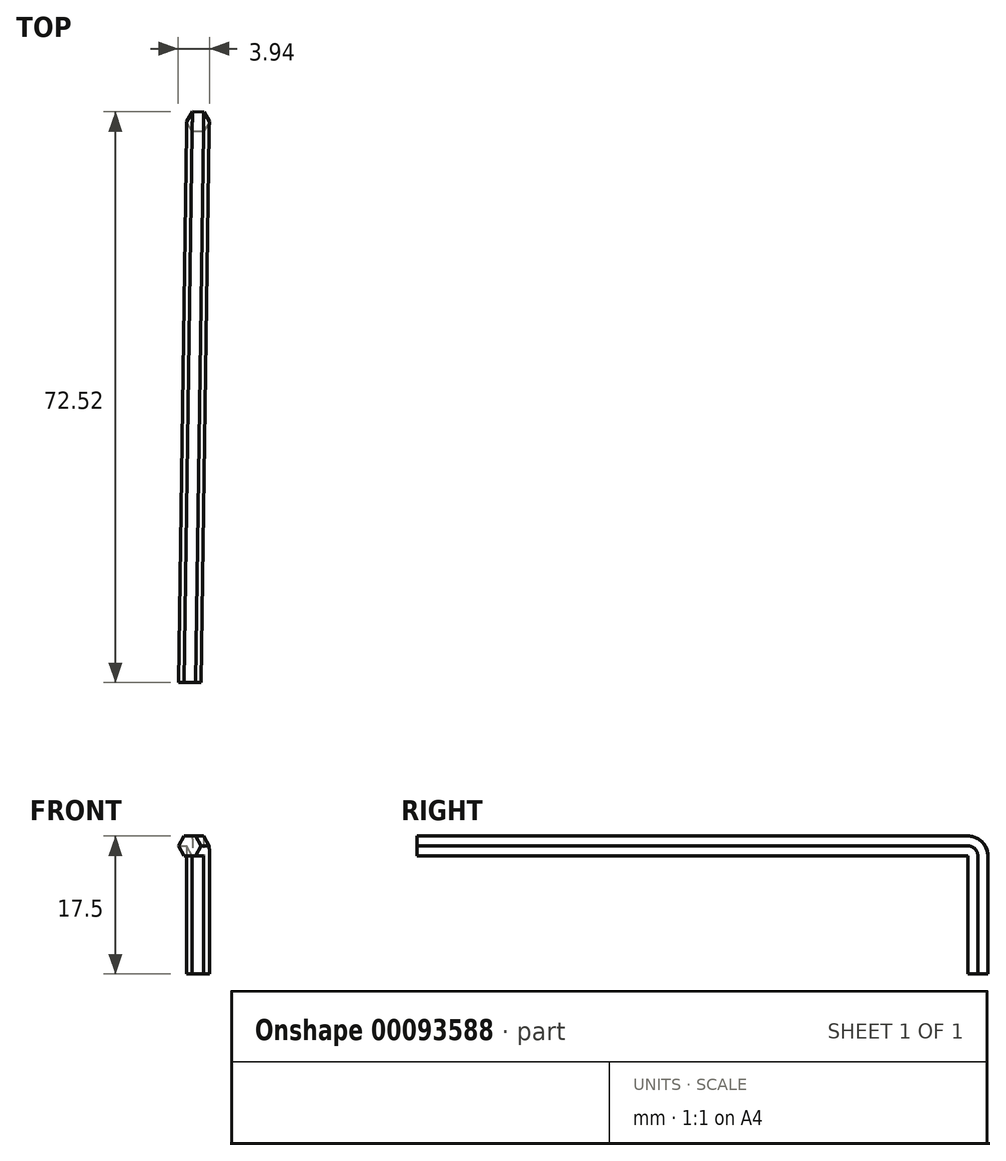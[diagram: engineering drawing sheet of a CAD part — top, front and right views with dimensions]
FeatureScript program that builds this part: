
annotation { "Feature Type Name" : "Feature", "Feature Type Description" : "" }
export const myFeature = defineFeature(function(context is Context, id is Id, definition is map)
    precondition{}
    {
        {
            var Q0;
            Q0=qCreatedBy(makeId("Top.planeOp"),FACE);
            var sketch = newSketch(context, id + "F0", { "sketchPlane" : qUnion([Q0])});
            skCircle(sketch, "E0.cCircle", {"center": v(0, 0) * mm, "radius": 1.25 * mm, "construction": true});
            skLineSegment(sketch, "E0.0", {"start": v(1.44, -0.02) * mm, "end": v(0.7, -1.26) * mm});
            skLineSegment(sketch, "E0.1", {"start": v(0.7, -1.26) * mm, "end": v(-0.74, -1.24) * mm});
            skLineSegment(sketch, "E0.2", {"start": v(-0.74, -1.24) * mm, "end": v(-1.44, 0.02) * mm});
            skLineSegment(sketch, "E0.3", {"start": v(-1.44, 0.02) * mm, "end": v(-0.7, 1.26) * mm});
            skLineSegment(sketch, "E0.4", {"start": v(-0.7, 1.26) * mm, "end": v(0.74, 1.24) * mm});
            skLineSegment(sketch, "E0.5", {"start": v(0.74, 1.24) * mm, "end": v(1.44, -0.02) * mm});
            skPoint(sketch, "E0.0.midPoint", {"position": v(1.07, -0.64) * mm});
            skSolve(sketch);
        }
        {
            var Q0;
            Q0=makeQuery(id+"F0.imprint","IMPRINT",FACE,{"disambiguationData":[TD([[makeQuery(id+"F0.imprint","IMPRINT",EDGE,{"derivedFrom":sQuery(id+"F0.wireOp",EDGE,"E0.0")}),-1.0]])]});
            extrude(context, id + "F1", {"entities" : qUnion([Q0]), "depth" : 15 * mm});
        }
        {
            var Q0;
            Q0=makeQuery(id+"F1.opExtrude","CAP_FACE",FACE,{"disambiguationData":[OSD([sQuery(id+"F0.wireOp",EDGE,"E0.0"),sQuery(id+"F0.wireOp",EDGE,"E0.1"),sQuery(id+"F0.wireOp",EDGE,"E0.2"),sQuery(id+"F0.wireOp",EDGE,"E0.3"),sQuery(id+"F0.wireOp",EDGE,"E0.4"),sQuery(id+"F0.wireOp",EDGE,"E0.5")])],"isStart":false});
            var sketch = newSketch(context, id + "F2", { "sketchPlane" : qUnion([Q0])});
            skSolve(sketch);
        }
        {
            var Q0;
            Q0=makeQuery(id+"F2.imprint","IMPRINT",FACE,{"disambiguationData":[TD([[makeQuery(id+"F2.imprint","IMPRINT",EDGE,{"derivedFrom":makeQuery(id+"F1.opExtrude","CAP_EDGE",EDGE,{"disambiguationData":[OSD([sQuery(id+"F0.wireOp",EDGE,"E0.0")])],"isStart":false})}),-1.0]])]});
            var Q1;
            Q1=makeQuery(id+"F1.opExtrude","CAP_EDGE",EDGE,{"disambiguationData":[OSD([sQuery(id+"F0.wireOp",EDGE,"E0.1")])],"isStart":false});
            revolve(context, id + "F3", {"operationType" : NewBodyOperationType.ADD, "entities" : qUnion([Q0]), "axis" : qUnion([Q1]), "revolveType" : RevolveType.ONE_DIRECTION, "oppositeDirection" : true, "angle" : 90 * degree});
        }
        {
            var Q0;
            {var subQ0=sQuery(id+"F0.wireOp",EDGE,"E0.1");Q0=makeQuery(id+"F3.boolean.opBoolean","MERGE",FACE,{"derivedFrom":[makeQuery(id+"F1.opExtrude","SWEPT_FACE",FACE,{"disambiguationData":[OSD([subQ0])]}),makeQuery(id+"F3.opRevolve","CAP_FACE",FACE,{"disambiguationData":[OSD([sQuery(id+"F0.wireOp",EDGE,"E0.0"),subQ0,sQuery(id+"F0.wireOp",EDGE,"E0.2"),sQuery(id+"F0.wireOp",EDGE,"E0.3"),sQuery(id+"F0.wireOp",EDGE,"E0.4"),sQuery(id+"F0.wireOp",EDGE,"E0.5")])],"isStart":false})]});}
            var sketch = newSketch(context, id + "F4", { "sketchPlane" : qUnion([Q0])});
            skLineSegment(sketch, "E1", {"start": v(0.72, 15) * mm, "end": v(-0.72, 15) * mm});
            skSolve(sketch);
        }
        {
            var Q0;
            Q0=makeQuery(id+"F4.imprint","IMPRINT",FACE,{"disambiguationData":[TD([[makeQuery(id+"F4.imprint","IMPRINT",EDGE,{"derivedFrom":sQuery(id+"F4.wireOp",EDGE,"E1")}),-1.0]])]});
            extrude(context, id + "F5", {"entities" : qUnion([Q0]), "operationType" : NewBodyOperationType.ADD, "depth" : 70 * mm});
        }
    });
